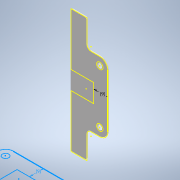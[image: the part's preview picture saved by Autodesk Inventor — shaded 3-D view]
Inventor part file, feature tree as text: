
AUTODESK INVENTOR PART (.ipt)
format: ipt  version: 2022 (Build 260153000, 153)  size: 140,288 bytes
history: native  units: mm
features: other x4, reference x2, extrude x1, fillet x1, sketch x1
ambient origin geometry x8: Origin, YZ Plane, XZ Plane, XY Plane, X Axis, Y Axis, Z Axis, Center Point
bodies: Body1 (feature_tree)
feature tree (9):
  other  "Твердое тело1"
  extrude  "Выдавливание1"  Depth=1.0mm TaperAngle=0.0deg
  fillet  "Сопряжение1"  Radius=1.0mm
  sketch  "Эскиз2"
  reference  "Ссылка2"
  reference  "Ссылка3"
  other  "<userpath>\Documents\Git\MZCAT_2024_construction\MZCAT_2024\MZCAT_4.iam"
  other  "MZCAT_4.iam"
  other  "base:1"
